# Revit family: Flopro Z3 Circular
name_source: partatom
category: Luminarias
revit_build: Autodesk Revit 2015 (Build: 20140606_1530(x64)
units: mm (PartAtom-declared; Revit-internal decimal feet)

## types (6) — shared parameters
Cambio de temperatura de color de luz atenuada = <Ninguno>
Fabricante = SECOM ILUMINACIÓN
Filtro de color = 16777215
Forma visible en renderización = No
Lámpara = LED Osram Duris
Ángulo de inclinación = 90.00°

## per-type parameters (varying)
| type | Archivo de red fotométrica | Comentarios de vataje | Descripción | Diámetro de círculo de emisión | Modelo | Óptica angulo de apertura |
| Flopro Z3 Circular  20W / 48º | 6150 00 20 84 FLOPRO Z3 LED CIRCULAR L48º 20W.IES | 20W | 6150 00 20 84 | 97 mm | Flopro Z2 Circular 20W | 48.00° |
| Flopro Z3 Circular 28W / 11º | 6150 00 30 84 11 FLOPRO Z3 LED CIRCULAR L11º 28W.IES | 28W | 6120 00 06 84 11 | 170 mm | Flopro Z2 Circular 6W | 11.00° |
| Flopro Z3 Circular 28W / 48º | 6150 00 30 84 FLOPRO Z3 LED CIRCULAR L48º 28W.IES | 28W | 6110 00 30 84 | 170 mm | Flopro Z3 Circular | 48.00° |
| Flopro Z3 Circular 20W / 11º | 6150 00 20 84 11 FLOPRO Z3 LED CIRCULAR L11º 20W.IES | 28W | 6120 00 06 84 11 | 170 mm | Flopro Z3 Circular 20W | 11.00° |
| Flopro Z3 asimétrico Circular 22W / 48º | 6180 00 22 84 FLOPRO Z3 LED CIRCULAR ASIMETRICO L48º 22W.IES | 22W | 6180 00 22 84 | 170 mm | Flopro Z3 Circular | 48.00° |
| Flopro Z3 asimétrico Circular 22W / 11º | 6180 00 22 84 11 FLOPRO Z3 LED CIRCULAR ASIMETRICO L11º 22W.IES | 22W | 6180 00 22 8411 | 170 mm | Flopro Z3 Circular | 11.00° |
